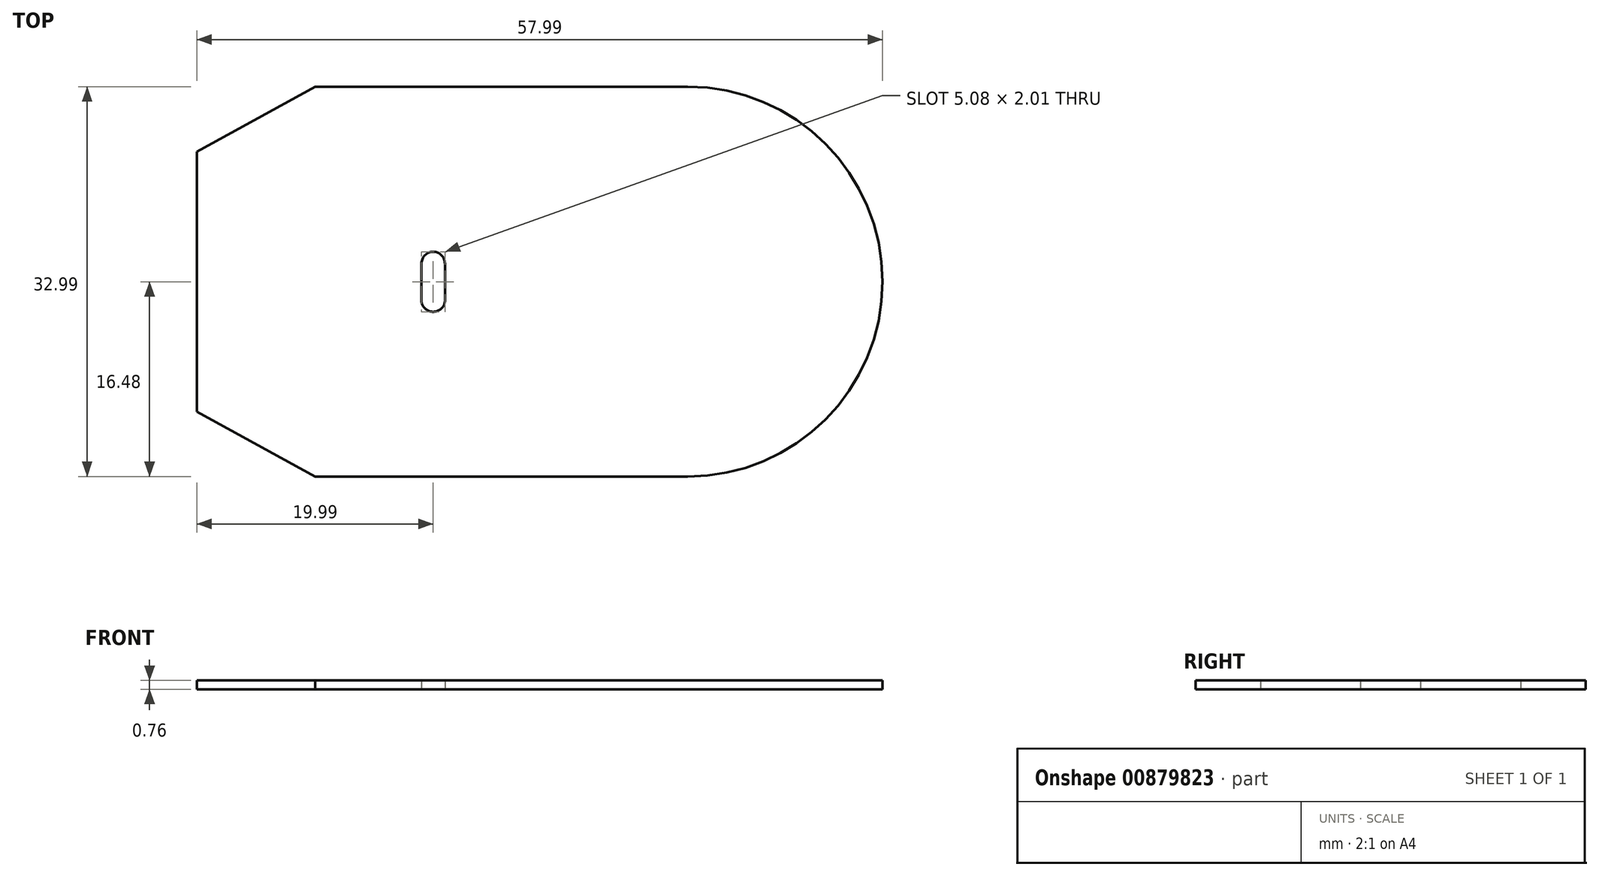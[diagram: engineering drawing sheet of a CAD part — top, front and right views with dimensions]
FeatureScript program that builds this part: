
annotation { "Feature Type Name" : "Feature", "Feature Type Description" : "" }
export const myFeature = defineFeature(function(context is Context, id is Id, definition is map)
    precondition{}
    {
        {
            var Q0;
            Q0=qCreatedBy(makeId("Top.planeOp"),FACE);
            var sketch = newSketch(context, id + "F0", { "sketchPlane" : qUnion([Q0])});
            skLineSegment(sketch, "E0.bottom", {"start": v(10, 0) * mm, "end": v(41.5, 0) * mm});
            skLineSegment(sketch, "E0.top", {"start": v(10, -33) * mm, "end": v(41.5, -33) * mm});
            skLineSegment(sketch, "E0.left", {"start": v(0, -6.67) * mm, "end": v(0, -27.5) * mm});
            skArc(sketch, "E1", {"start": v(41.5, 0) * mm, "mid": v(57.99, -16.5) * mm, "end": v(41.5, -33) * mm});
            skPoint(sketch, "E2", {"position": v(57.99, -16.5) * mm});
            skPoint(sketch, "E3", {"position": v(0, -5.49) * mm});
            skPoint(sketch, "E4", {"position": v(0, -27.5) * mm});
            skPoint(sketch, "E5", {"position": v(10, 0) * mm});
            skPoint(sketch, "E6", {"position": v(10, -33) * mm});
            skLineSegment(sketch, "E7", {"start": v(1.04, -4.92) * mm, "end": v(10, 0) * mm});
            skLineSegment(sketch, "E8", {"start": v(0, -27.5) * mm, "end": v(10, -33) * mm});
            skPoint(sketch, "E9.orphan", {"position": v(0, 0) * mm});
            skPoint(sketch, "E10.orphan", {"position": v(0, -33) * mm});
            skArc(sketch, "E11.0.startCap", {"start": v(19, -14.96) * mm, "mid": v(19.99, -13.97) * mm, "end": v(20.98, -14.96) * mm});
            skArc(sketch, "E11.0.endCap", {"start": v(21, -18.04) * mm, "mid": v(19.99, -19.05) * mm, "end": v(18.99, -18.04) * mm});
            skLineSegment(sketch, "E11.0.left", {"start": v(20.98, -14.96) * mm, "end": v(21, -18.04) * mm});
            skLineSegment(sketch, "E11.0.right", {"start": v(19, -14.96) * mm, "end": v(18.99, -18.04) * mm});
            skPoint(sketch, "E12.positionSnap0", {"position": v(19, -16.5) * mm});
            skLineSegment(sketch, "E13", {"start": v(19.99, -13.97) * mm, "end": v(19.99, -19.05) * mm});
            skPoint(sketch, "E13.startSnap0", {"position": v(19.99, -13.97) * mm});
            skPoint(sketch, "E13.endSnap0", {"position": v(19.99, -19.05) * mm});
            skPoint(sketch, "E14", {"position": v(19.99, -16.51) * mm});
            skLineSegment(sketch, "E15", {"start": v(1.04, -4.92) * mm, "end": v(0, -5.49) * mm});
            skLineSegment(sketch, "E16", {"start": v(0, -6.67) * mm, "end": v(0, -5.49) * mm});
            skSolve(sketch);
        }
        {
            var Q0;
            Q0=makeQuery(id+"F0.imprint","IMPRINT",FACE,{"disambiguationData":[TD([[makeQuery(id+"F0.imprint","IMPRINT",EDGE,{"derivedFrom":sQuery(id+"F0.wireOp",EDGE,"E0.bottom")}),-1.0]])]});
            extrude(context, id + "F1", {"entities" : qUnion([Q0]), "depth" : 0.76 * mm, "offsetDistance" : 25.4 * mm});
        }
    });
